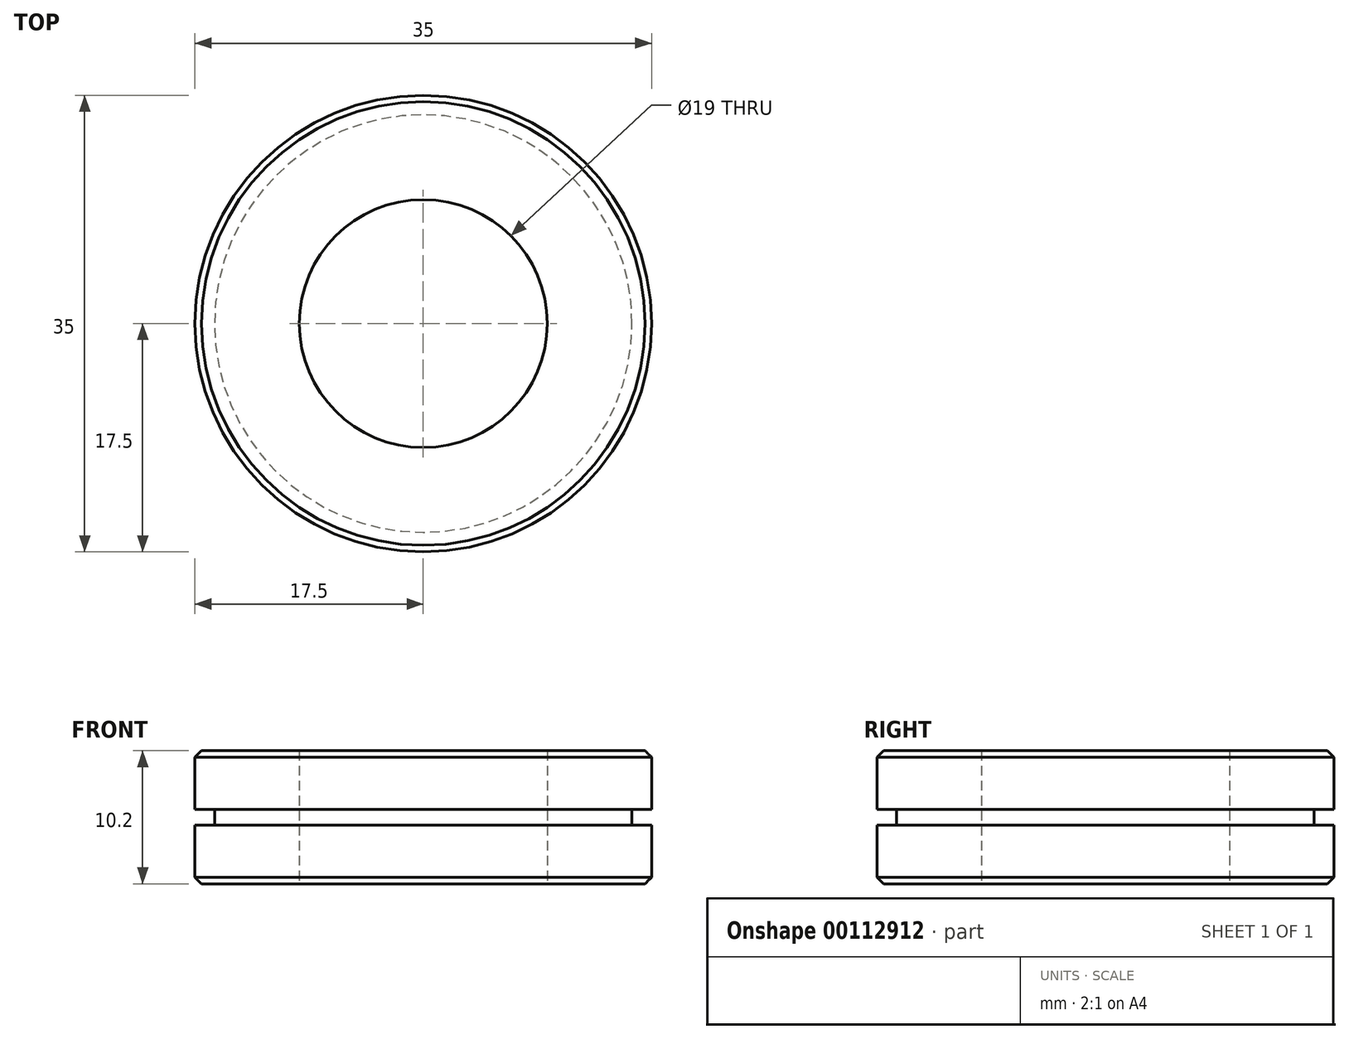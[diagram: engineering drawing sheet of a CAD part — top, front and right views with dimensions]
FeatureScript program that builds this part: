
annotation { "Feature Type Name" : "Feature", "Feature Type Description" : "" }
export const myFeature = defineFeature(function(context is Context, id is Id, definition is map)
    precondition{}
    {
        {
            var Q0;
            Q0=qCreatedBy(makeId("Top.planeOp"),FACE);
            var sketch = newSketch(context, id + "F0", { "sketchPlane" : qUnion([Q0])});
            skCircle(sketch, "E0", {"center": v(0, 0) * mm, "radius": 17.5 * mm});
            skCircle(sketch, "E1", {"center": v(0, 0) * mm, "radius": 9.5 * mm});
            skSolve(sketch);
        }
        {
            var Q0;
            Q0 = qSketchRegion(id + "F0", true);
            extrude(context, id + "F1", {"entities" : qUnion([Q0]), "depth" : 4.5 * mm});
        }
        {
            var Q0;
            Q0=makeQuery(id+"F1.opExtrude","CAP_FACE",FACE,{"disambiguationData":[OSD([sQuery(id+"F0.wireOp",EDGE,"E0"),sQuery(id+"F0.wireOp",EDGE,"E1")])],"isStart":false});
            var sketch = newSketch(context, id + "F2", { "sketchPlane" : qUnion([Q0])});
            skCircle(sketch, "E2", {"center": v(0, 0) * mm, "radius": 9.5 * mm});
            skCircle(sketch, "E3", {"center": v(0, 0) * mm, "radius": 16 * mm});
            skSolve(sketch);
        }
        {
            var Q0;
            Q0 = qSketchRegion(id + "F2", true);
            extrude(context, id + "F3", {"entities" : qUnion([Q0]), "operationType" : NewBodyOperationType.ADD, "depth" : 1.2 * mm});
        }
        {
            var Q0;
            Q0=makeQuery(id+"F3.opExtrude","CAP_FACE",FACE,{"disambiguationData":[OSD([sQuery(id+"F2.wireOp",EDGE,"E2"),sQuery(id+"F2.wireOp",EDGE,"E3")])],"isStart":false});
            var sketch = newSketch(context, id + "F4", { "sketchPlane" : qUnion([Q0])});
            skCircle(sketch, "E4", {"center": v(0, 0) * mm, "radius": 9.5 * mm});
            skCircle(sketch, "E5", {"center": v(0, 0) * mm, "radius": 17.5 * mm});
            skSolve(sketch);
        }
        {
            var Q0;
            Q0 = qSketchRegion(id + "F4", true);
            extrude(context, id + "F5", {"entities" : qUnion([Q0]), "operationType" : NewBodyOperationType.ADD, "depth" : 4.5 * mm});
        }
        {
            var Q0;
            Q0=makeQuery(id+"F5.opExtrude","CAP_EDGE",EDGE,{"disambiguationData":[OSD([sQuery(id+"F4.wireOp",EDGE,"E5")])],"isStart":false});
            var Q1;
            Q1=makeQuery(id+"F1.opExtrude","CAP_EDGE",EDGE,{"disambiguationData":[OSD([sQuery(id+"F0.wireOp",EDGE,"E0")])],"isStart":true});
            chamfer(context, id + "F6", {"entities" : qUnion([Q0, Q1]), "width" : .5 * mm, "tangentPropagation" : true});
        }
    });
